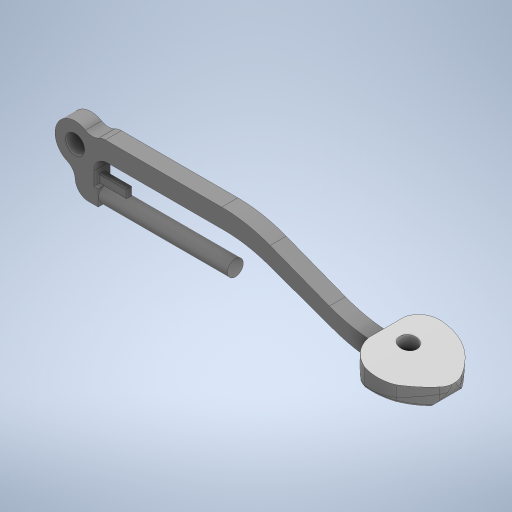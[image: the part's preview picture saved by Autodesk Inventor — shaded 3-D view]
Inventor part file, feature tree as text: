
AUTODESK INVENTOR PART (.ipt)
format: ipt  version: 2024 (Build 280153000, 153)  size: 801,792 bytes
history: native  units: mm
features: other x3, plane x2, extrude x2, sketch x2
ambient origin geometry x8: Origin, YZ Plane, XZ Plane, XY Plane, X Axis, Y Axis, Z Axis, Center Point
bodies: Body1 (feature_tree)
feature tree (9):
  other  "Tubo.ipt"
  plane  "Plano de trabajo1"
  extrude  "Extrusión1"  Depth=38.0mm
  plane  "Plano de trabajo2"
  extrude  "Extrusión2"  Depth=15.0mm
  other  "Sólido2::Tubo.ipt"
  other  "OperaciónIdentificador1"
  sketch  "Boceto1"  dims[d0=25.0mm d1=38.0mm]
  sketch  "Boceto2"  dims[d2=100.0mm d3=0.0mm d4=20.0mm d5=20.0mm d6=16.0mm d7=15.0mm d8=0.0mm]
